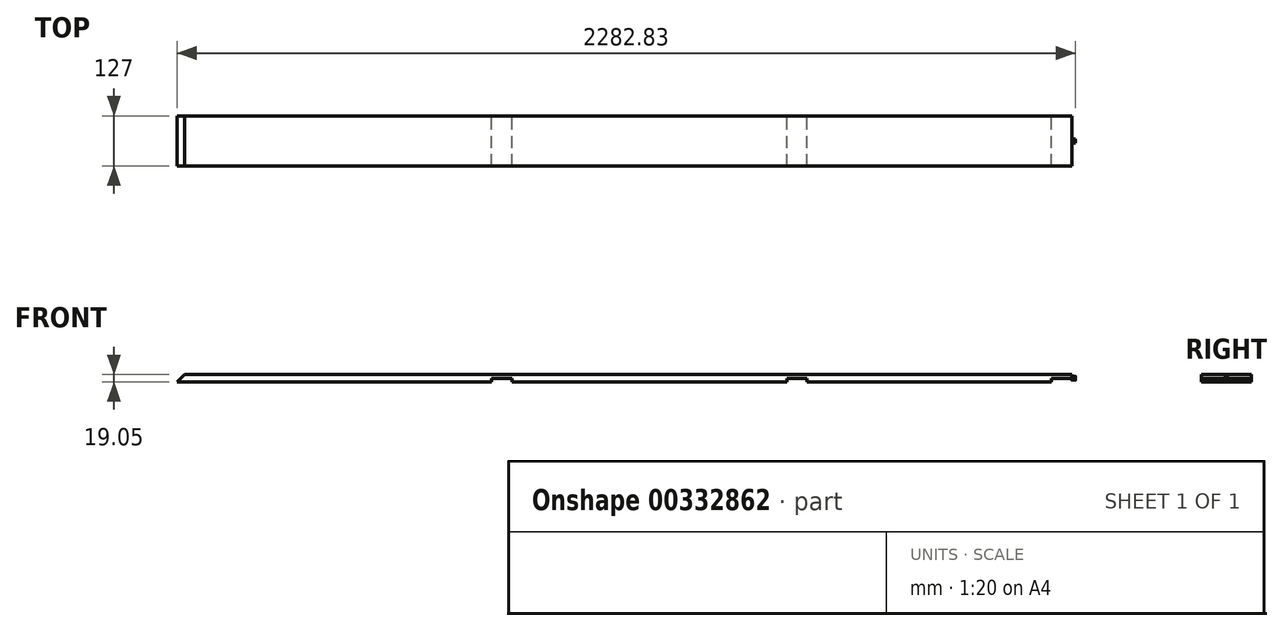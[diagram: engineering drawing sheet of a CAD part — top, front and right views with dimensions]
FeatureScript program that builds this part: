
annotation { "Feature Type Name" : "Feature", "Feature Type Description" : "" }
export const myFeature = defineFeature(function(context is Context, id is Id, definition is map)
    precondition{}
    {
        {
            var Q0;
            Q0=qCreatedBy(makeId("Front.planeOp"),FACE);
            var sketch = newSketch(context, id + "F0", { "sketchPlane" : qUnion([Q0])});
            skLineSegment(sketch, "E0.bottom", {"start": v(25.4, 0) * mm, "end": v(800.1, 0) * mm});
            skLineSegment(sketch, "E0.right", {"start": v(2273.3, 9.52) * mm, "end": v(2273.3, 19.05) * mm});
            skLineSegment(sketch, "E1", {"start": v(2273.3, 19.05) * mm, "end": v(19.05, 19.05) * mm});
            skPoint(sketch, "E2.left.start.orphan", {"position": v(-798.41, -3.82) * mm});
            skLineSegment(sketch, "E3.top", {"start": v(800.1, 9.52) * mm, "end": v(850.9, 9.52) * mm});
            skLineSegment(sketch, "E3.left", {"start": v(800.1, 0) * mm, "end": v(800.1, 9.52) * mm});
            skLineSegment(sketch, "E3.right", {"start": v(850.9, 0) * mm, "end": v(850.9, 9.52) * mm});
            skLineSegment(sketch, "E4.trimOffspring", {"start": v(850.9, 0) * mm, "end": v(1549.4, 0) * mm});
            skLineSegment(sketch, "E5.top", {"start": v(1549.4, 9.52) * mm, "end": v(1600.2, 9.52) * mm});
            skLineSegment(sketch, "E5.left", {"start": v(1549.4, 0) * mm, "end": v(1549.4, 9.52) * mm});
            skLineSegment(sketch, "E5.right", {"start": v(1600.2, 0) * mm, "end": v(1600.2, 9.52) * mm});
            skLineSegment(sketch, "E6.trimOffspring", {"start": v(1600.2, 0) * mm, "end": v(2222.5, 0) * mm});
            skLineSegment(sketch, "E7.top", {"start": v(2222.5, 9.52) * mm, "end": v(2273.3, 9.52) * mm});
            skLineSegment(sketch, "E7.left", {"start": v(2222.5, 0) * mm, "end": v(2222.5, 9.52) * mm});
            skPoint(sketch, "E8.orphan", {"position": v(2273.3, 0) * mm});
            skLineSegment(sketch, "E9", {"start": v(25.4, 0) * mm, "end": v(0, 0) * mm});
            skLineSegment(sketch, "E10", {"start": v(0, 0) * mm, "end": v(19.05, 19.05) * mm});
            skSolve(sketch);
        }
        {
            var Q0;
            Q0=qSketchRegion(id+"F0",true);
            extrude(context, id + "F1", {"entities" : qUnion([Q0]), "endBound" : BoundingType.SYMMETRIC, "depth" : 127 * mm});
        }
        {
            var Q0;
            Q0=qCreatedBy(makeId("Right.planeOp"),FACE);
            cPlane(context, id + "F2", {"entities" : qUnion([Q0]), "cplaneType" : CPlaneType.OFFSET, "offset" : 2273.3 * mm, "width" : 152.4 * mm, "height" : 152.4 * mm});
        }
        {
            var Q0;
            Q0=qCreatedBy(id+"F2.planeOp",FACE);
            var sketch = newSketch(context, id + "F3", { "sketchPlane" : qUnion([Q0])});
            skCircle(sketch, "E11", {"center": v(0, 9.52) * mm, "radius": 4.76 * mm});
            skSolve(sketch);
        }
        {
            var Q0;
            Q0=qSketchRegion(id+"F3",true);
            extrude(context, id + "F4", {"entities" : qUnion([Q0]), "operationType" : NewBodyOperationType.ADD, "depth" : 9.52 * mm});
        }
    });
